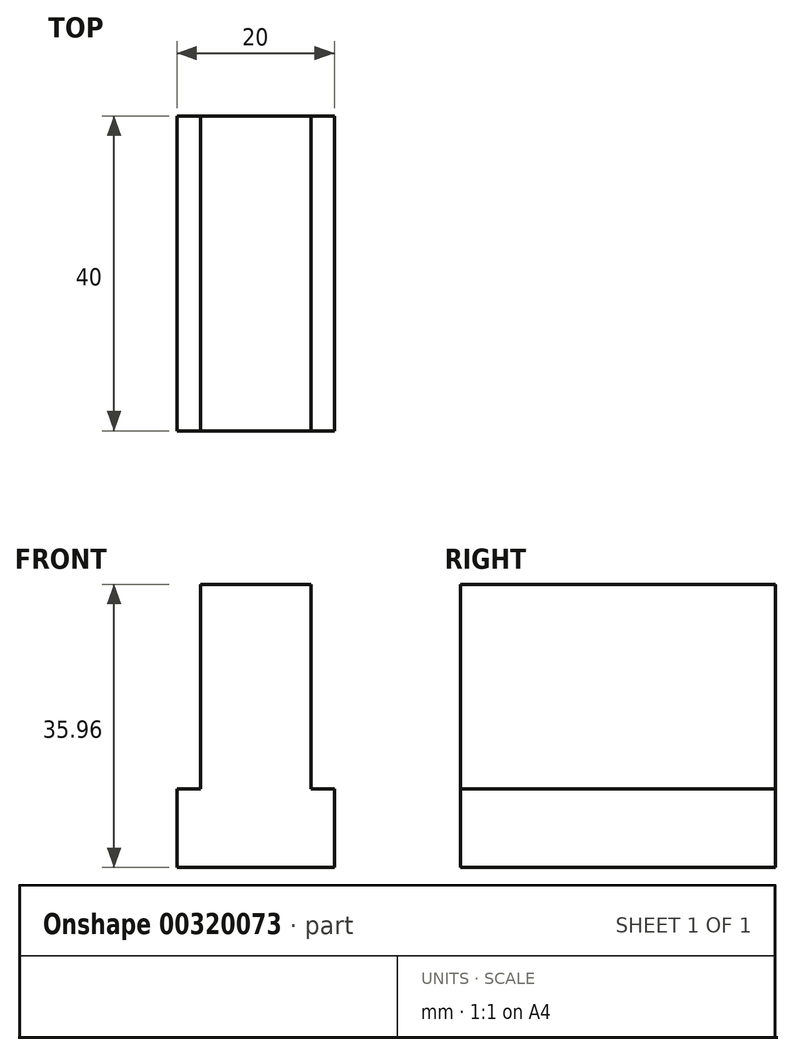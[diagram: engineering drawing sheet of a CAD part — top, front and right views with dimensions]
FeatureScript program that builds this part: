
annotation { "Feature Type Name" : "Feature", "Feature Type Description" : "" }
export const myFeature = defineFeature(function(context is Context, id is Id, definition is map)
    precondition{}
    {
        {
            var Q0;
            Q0=qCreatedBy(makeId("Front.planeOp"),FACE);
            var sketch = newSketch(context, id + "F0", { "sketchPlane" : qUnion([Q0])});
            skLineSegment(sketch, "E0.bottom", {"start": v(-7, 0) * mm, "end": v(-10, 0) * mm});
            skLineSegment(sketch, "E0.top", {"start": v(0, -10) * mm, "end": v(-10, -10) * mm});
            skLineSegment(sketch, "E0.right", {"start": v(-10, 0) * mm, "end": v(-10, -10) * mm});
            skLineSegment(sketch, "E1.right", {"start": v(-7, 0) * mm, "end": v(-7, 25.96) * mm});
            skLineSegment(sketch, "E2", {"start": v(0, 25.96) * mm, "end": v(0, -10) * mm});
            skLineSegment(sketch, "E3", {"start": v(-7, 25.96) * mm, "end": v(0, 25.96) * mm});
            skSolve(sketch);
        }
        {
            var Q0;
            Q0=makeQuery(id+"F0.imprint","IMPRINT",FACE,{"disambiguationData":[TD([[makeQuery(id+"F0.imprint","IMPRINT",EDGE,{"derivedFrom":sQuery(id+"F0.wireOp",EDGE,"E0.bottom")}),1.0]])]});
            extrude(context, id + "F1", {"entities" : qUnion([Q0]), "endBound" : BoundingType.SYMMETRIC, "depth" : 40 * mm});
        }
        {
            var Q0;
            Q0=makeQuery(id+"F1.opExtrude","SWEPT_BODY",BODY,{"disambiguationData":[OSD([sQuery(id+"F0.wireOp",EDGE,"E0.bottom"),sQuery(id+"F0.wireOp",EDGE,"E0.top"),sQuery(id+"F0.wireOp",EDGE,"E0.right"),sQuery(id+"F0.wireOp",EDGE,"E1.right"),sQuery(id+"F0.wireOp",EDGE,"E2"),sQuery(id+"F0.wireOp",EDGE,"E3")])]});
            var Q1;
            Q1=makeQuery(id+"F1.opExtrude","SWEPT_FACE",FACE,{"disambiguationData":[OSD([sQuery(id+"F0.wireOp",EDGE,"E2")])]});
            mirror(context, id + "F2", {"operationType" : NewBodyOperationType.ADD, "entities" : qUnion([Q0]), "mirrorPlane" : qUnion([Q1])});
        }
    });
